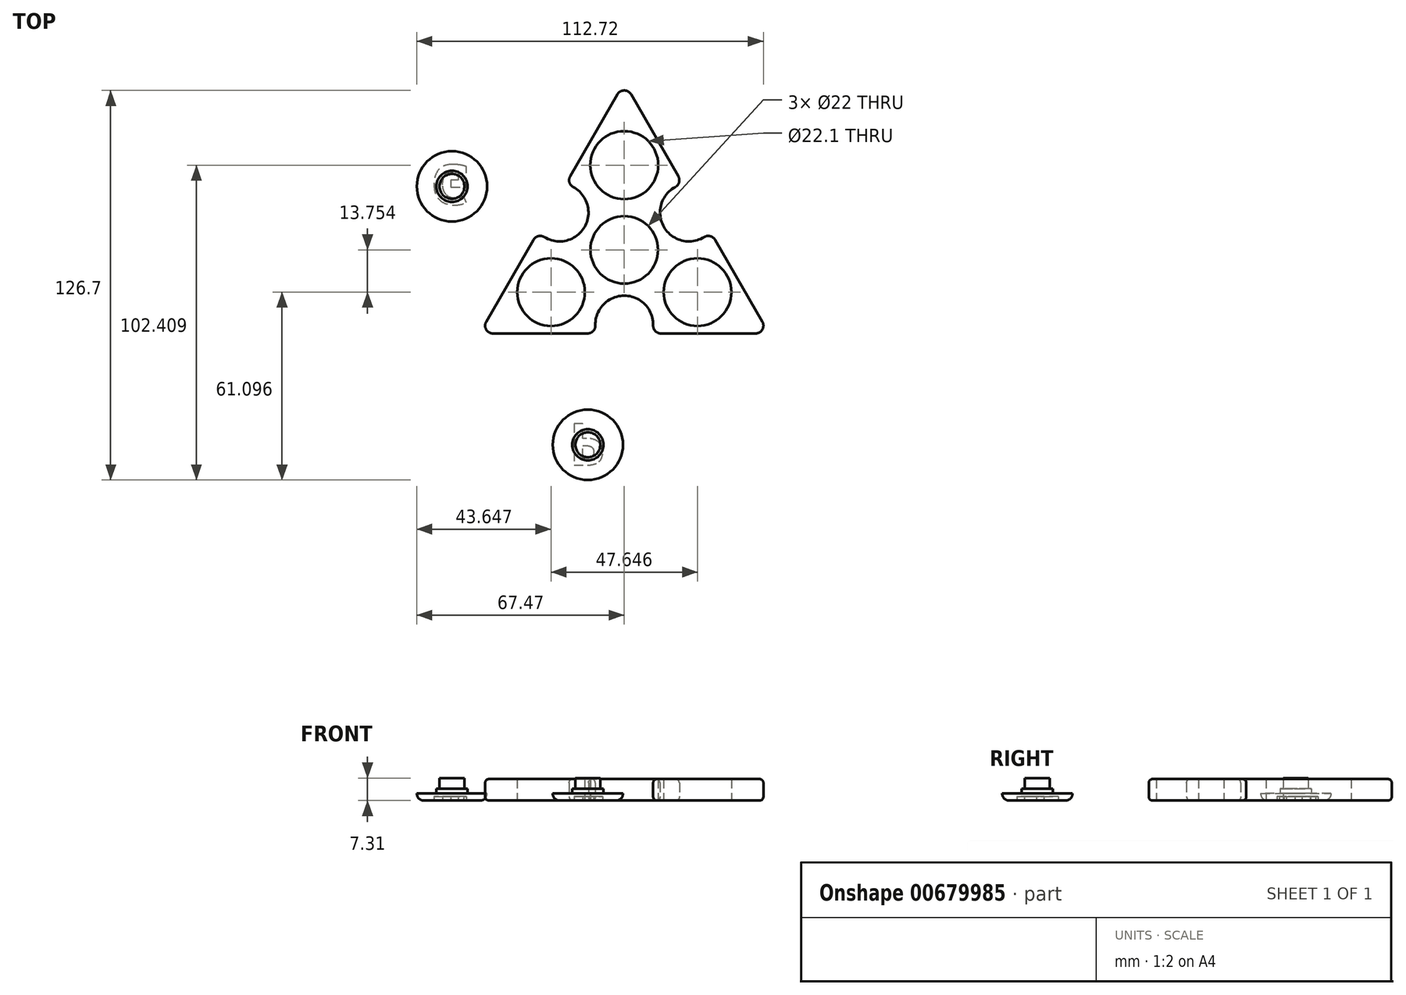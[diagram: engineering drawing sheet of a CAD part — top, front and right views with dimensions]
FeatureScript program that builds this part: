
annotation { "Feature Type Name" : "Feature", "Feature Type Description" : "" }
export const myFeature = defineFeature(function(context is Context, id is Id, definition is map)
    precondition{}
    {
        {
            var Q0;
            Q0=qCreatedBy(makeId("Top.planeOp"),FACE);
            var sketch = newSketch(context, id + "F0", { "sketchPlane" : qUnion([Q0])});
            skCircle(sketch, "E0", {"center": v(0, 42.8) * mm, "radius": 11.05 * mm});
            skCircle(sketch, "E1.1.2", {"center": v(-23.82, 1.49) * mm, "radius": 11 * mm});
            skCircle(sketch, "E1.2.2", {"center": v(23.82, 1.49) * mm, "radius": 11 * mm});
            skPoint(sketch, "E1.center", {"position": v(0, 15.24) * mm});
            skArc(sketch, "E2", {"start": v(19.08, 36.58) * mm, "mid": v(12.9, 22.69) * mm, "end": v(28.02, 21.1) * mm});
            skArc(sketch, "E3.1.0", {"start": v(-28.02, 21.1) * mm, "mid": v(-12.9, 22.69) * mm, "end": v(-19.08, 36.58) * mm});
            skArc(sketch, "E3.2.0", {"start": v(8.94, -11.96) * mm, "mid": v(0, 0.34) * mm, "end": v(-8.94, -11.96) * mm});
            skLineSegment(sketch, "E4", {"start": v(8.94, -11.96) * mm, "end": v(47.1, -11.96) * mm});
            skLineSegment(sketch, "E5", {"start": v(28.02, 21.1) * mm, "end": v(47.1, -11.96) * mm});
            skLineSegment(sketch, "E6", {"start": v(-47.1, -11.96) * mm, "end": v(-8.94, -11.96) * mm});
            skLineSegment(sketch, "E7", {"start": v(-47.1, -11.96) * mm, "end": v(-28.02, 21.1) * mm});
            skLineSegment(sketch, "E8", {"start": v(-19.08, 36.58) * mm, "end": v(0, 69.63) * mm});
            skLineSegment(sketch, "E9", {"start": v(0, 69.63) * mm, "end": v(19.08, 36.58) * mm});
            skCircle(sketch, "E10", {"center": v(0, 15.24) * mm, "radius": 11 * mm});
            skSolve(sketch);
        }
        {
            var Q0;
            Q0 = qSketchRegion(id + "F0", true);
            extrude(context, id + "F1", {"entities" : qUnion([Q0]), "flatOperationType" : FlatOperationType.REMOVE, "depth" : 7 * mm, "offsetDistance" : 25.4 * mm, "domain" : OperationDomain.MODEL});
        }
        {
            var Q0;
            Q0=makeQuery(id+"F1.opExtrude","SWEPT_EDGE",EDGE,{"disambiguationData":[OSD([sQuery(id+"F0.wireOp",EDGE,"E4"),sQuery(id+"F0.wireOp",EDGE,"E5")])]});
            var Q1;
            Q1=makeQuery(id+"F1.opExtrude","SWEPT_EDGE",EDGE,{"disambiguationData":[OSD([sQuery(id+"F0.wireOp",EDGE,"E3.2.0"),sQuery(id+"F0.wireOp",EDGE,"E4")])]});
            var Q2;
            Q2=makeQuery(id+"F1.opExtrude","SWEPT_EDGE",EDGE,{"disambiguationData":[OSD([sQuery(id+"F0.wireOp",EDGE,"E3.2.0"),sQuery(id+"F0.wireOp",EDGE,"E6")])]});
            var Q3;
            Q3=makeQuery(id+"F1.opExtrude","SWEPT_EDGE",EDGE,{"disambiguationData":[OSD([sQuery(id+"F0.wireOp",EDGE,"E6"),sQuery(id+"F0.wireOp",EDGE,"E7")])]});
            var Q4;
            Q4=makeQuery(id+"F1.opExtrude","SWEPT_EDGE",EDGE,{"disambiguationData":[OSD([sQuery(id+"F0.wireOp",EDGE,"E3.1.0"),sQuery(id+"F0.wireOp",EDGE,"E7")])]});
            var Q5;
            Q5=makeQuery(id+"F1.opExtrude","SWEPT_EDGE",EDGE,{"disambiguationData":[OSD([sQuery(id+"F0.wireOp",EDGE,"E3.1.0"),sQuery(id+"F0.wireOp",EDGE,"E8")])]});
            var Q6;
            Q6=makeQuery(id+"F1.opExtrude","SWEPT_EDGE",EDGE,{"disambiguationData":[OSD([sQuery(id+"F0.wireOp",EDGE,"E8"),sQuery(id+"F0.wireOp",EDGE,"E9")])]});
            var Q7;
            Q7=makeQuery(id+"F1.opExtrude","SWEPT_EDGE",EDGE,{"disambiguationData":[OSD([sQuery(id+"F0.wireOp",EDGE,"E2"),sQuery(id+"F0.wireOp",EDGE,"E5")])]});
            var Q8;
            Q8=makeQuery(id+"F1.opExtrude","SWEPT_EDGE",EDGE,{"disambiguationData":[OSD([sQuery(id+"F0.wireOp",EDGE,"E2"),sQuery(id+"F0.wireOp",EDGE,"E9")])]});
            fillet(context, id + "F2", {"entities" : qUnion([Q0, Q1, Q2, Q3, Q4, Q5, Q6, Q7, Q8]), "radius" : 2.54 * mm, "tangentPropagation" : true, "allowEdgeOverflow" : false});
        }
        {
            var Q0;
            Q0=qCreatedBy(makeId("Top.planeOp"),FACE);
            var sketch = newSketch(context, id + "F3", { "sketchPlane" : qUnion([Q0])});
            skCircle(sketch, "E11", {"center": v(-56.04, 35.9) * mm, "radius": 11.43 * mm});
            skSolve(sketch);
        }
        {
            var Q0;
            Q0=makeQuery(id+"F3.imprint","IMPRINT",FACE,{"disambiguationData":[TD([[makeQuery(id+"F3.imprint","IMPRINT",EDGE,{"derivedFrom":sQuery(id+"F3.wireOp",EDGE,"E11")}),1.0]])]});
            extrude(context, id + "F4", {"entities" : qUnion([Q0]), "depth" : 2.3 * mm, "offsetDistance" : 25.4 * mm});
        }
        {
            var Q0;
            Q0=makeQuery(id+"F4.opExtrude","CAP_EDGE",EDGE,{"disambiguationData":[OSD([sQuery(id+"F3.wireOp",EDGE,"E11")])],"isStart":true});
            fillet(context, id + "F5", {"entities" : qUnion([Q0]), "radius" : 2.3 * mm, "tangentPropagation" : true, "allowEdgeOverflow" : false});
        }
        {
            var Q0;
            Q0=makeQuery(id+"F4.opExtrude","SWEPT_BODY",BODY,{"disambiguationData":[OSD([sQuery(id+"F3.wireOp",EDGE,"E11")])]});
            transform(context, id + "F6", {"entities" : qUnion([Q0]), "transformType" : TransformType.TRANSLATION_3D, "dx" : 44.2 * mm, "dy" : -84.07 * mm, "dz" : 0 * mm, "makeCopy" : true});
        }
        {
            var Q0;
            Q0=makeQuery(id+"F4.opExtrude","CAP_FACE",FACE,{"disambiguationData":[OSD([sQuery(id+"F3.wireOp",EDGE,"E11")])],"isStart":true});
            var sketch = newSketch(context, id + "F7", { "sketchPlane" : qUnion([Q0])});
            skText(sketch, "E12", { "text": "G", "fontName": "OpenSans-Bold.ttf"});
            const initialGuessF7  = {"E12": [-0.06293, -0.04287, 1, 0, 0.013]};
            skSetInitialGuess(sketch, initialGuessF7);
            skSolve(sketch);
        }
        {
            var Q0;
            Q0 = qSketchRegion(id + "F7", true);
            extrude(context, id + "F8", {"entities" : qUnion([Q0]), "operationType" : NewBodyOperationType.REMOVE, "oppositeDirection" : true, "depth" : 1.27 * mm, "offsetDistance" : 25.4 * mm});
        }
        {
            var Q0;
            Q0=makeQuery(id+"F6.opPattern","COPY",FACE,{"derivedFrom":makeQuery(id+"F4.opExtrude","CAP_FACE",FACE,{"disambiguationData":[OSD([sQuery(id+"F3.wireOp",EDGE,"E11")])],"isStart":true}),"instanceName":"1"});
            var sketch = newSketch(context, id + "F9", { "sketchPlane" : qUnion([Q0])});
            skText(sketch, "E13", { "text": "P", "fontName": "OpenSans-Bold.ttf"});
            const initialGuessF9  = {"E13": [-0.01804, 0.0413, 1, 0, 0.0136]};
            skSetInitialGuess(sketch, initialGuessF9);
            skSolve(sketch);
        }
        {
            var Q0;
            Q0 = qSketchRegion(id + "F9", true);
            extrude(context, id + "F10", {"entities" : qUnion([Q0]), "operationType" : NewBodyOperationType.REMOVE, "oppositeDirection" : true, "depth" : 1.27 * mm, "offsetDistance" : 25.4 * mm});
        }
        {
            var Q0;
            Q0=makeQuery(id+"F6.opPattern","COPY",FACE,{"derivedFrom":makeQuery(id+"F4.opExtrude","CAP_FACE",FACE,{"disambiguationData":[OSD([sQuery(id+"F3.wireOp",EDGE,"E11")])],"isStart":false}),"instanceName":"1"});
            var sketch = newSketch(context, id + "F11", { "sketchPlane" : qUnion([Q0])});
            skCircle(sketch, "E14", {"center": v(-11.84, -48.18) * mm, "radius": 5.08 * mm});
            skSolve(sketch);
        }
        {
            var Q0;
            Q0=makeQuery(id+"F11.imprint","IMPRINT",FACE,{"disambiguationData":[TD([[makeQuery(id+"F11.imprint","IMPRINT",EDGE,{"derivedFrom":sQuery(id+"F11.wireOp",EDGE,"E14")}),1.0]])]});
            extrude(context, id + "F12", {"entities" : qUnion([Q0]), "operationType" : NewBodyOperationType.ADD, "depth" : 1.52 * mm, "offsetDistance" : 25.4 * mm});
        }
        {
            var Q0;
            Q0=makeQuery(id+"F4.opExtrude","CAP_FACE",FACE,{"disambiguationData":[OSD([sQuery(id+"F3.wireOp",EDGE,"E11")])],"isStart":false});
            var sketch = newSketch(context, id + "F13", { "sketchPlane" : qUnion([Q0])});
            skCircle(sketch, "E15", {"center": v(-56.04, 35.9) * mm, "radius": 5.08 * mm});
            skSolve(sketch);
        }
        {
            var Q0;
            Q0=makeQuery(id+"F13.imprint","IMPRINT",FACE,{"disambiguationData":[TD([[makeQuery(id+"F13.imprint","IMPRINT",EDGE,{"derivedFrom":sQuery(id+"F13.wireOp",EDGE,"E15")}),1.0]])]});
            extrude(context, id + "F14", {"entities" : qUnion([Q0]), "operationType" : NewBodyOperationType.ADD, "depth" : 1.52 * mm, "offsetDistance" : 25.4 * mm});
        }
        {
            var Q0;
            Q0=makeQuery(id+"F12.opExtrude","CAP_FACE",FACE,{"disambiguationData":[OSD([sQuery(id+"F11.wireOp",EDGE,"E14")])],"isStart":false});
            var sketch = newSketch(context, id + "F15", { "sketchPlane" : qUnion([Q0])});
            skCircle(sketch, "E16", {"center": v(-11.84, -48.18) * mm, "radius": 4.06 * mm});
            skSolve(sketch);
        }
        {
            var Q0;
            Q0=makeQuery(id+"F15.imprint","IMPRINT",FACE,{"disambiguationData":[TD([[makeQuery(id+"F15.imprint","IMPRINT",EDGE,{"derivedFrom":sQuery(id+"F15.wireOp",EDGE,"E16")}),1.0]])]});
            extrude(context, id + "F16", {"entities" : qUnion([Q0]), "operationType" : NewBodyOperationType.ADD, "depth" : 3.5 * mm, "offsetDistance" : 25.4 * mm});
        }
        {
            var Q0;
            Q0=makeQuery(id+"F14.opExtrude","CAP_FACE",FACE,{"disambiguationData":[OSD([sQuery(id+"F13.wireOp",EDGE,"E15")])],"isStart":false});
            var sketch = newSketch(context, id + "F17", { "sketchPlane" : qUnion([Q0])});
            skCircle(sketch, "E17", {"center": v(-56.04, 35.9) * mm, "radius": 4.06 * mm});
            skSolve(sketch);
        }
        {
            var Q0;
            Q0=makeQuery(id+"F17.imprint","IMPRINT",FACE,{"disambiguationData":[TD([[makeQuery(id+"F17.imprint","IMPRINT",EDGE,{"derivedFrom":sQuery(id+"F17.wireOp",EDGE,"E17")}),1.0]])]});
            extrude(context, id + "F18", {"entities" : qUnion([Q0]), "operationType" : NewBodyOperationType.ADD, "depth" : 3.5 * mm, "offsetDistance" : 25.4 * mm});
        }
        {
            var Q0;
            Q0=makeQuery(id+"F1.opExtrude","CAP_EDGE",EDGE,{"disambiguationData":[OSD([sQuery(id+"F0.wireOp",EDGE,"E3.2.0")])],"isStart":false});
            var Q1;
            Q1=makeQuery(id+"F1.opExtrude","CAP_EDGE",EDGE,{"disambiguationData":[OSD([sQuery(id+"F0.wireOp",EDGE,"E3.2.0")])],"isStart":true});
            fillet(context, id + "F19", {"entities" : qUnion([Q0, Q1]), "radius" : 1.27 * mm, "tangentPropagation" : true, "allowEdgeOverflow" : false});
        }
    });
